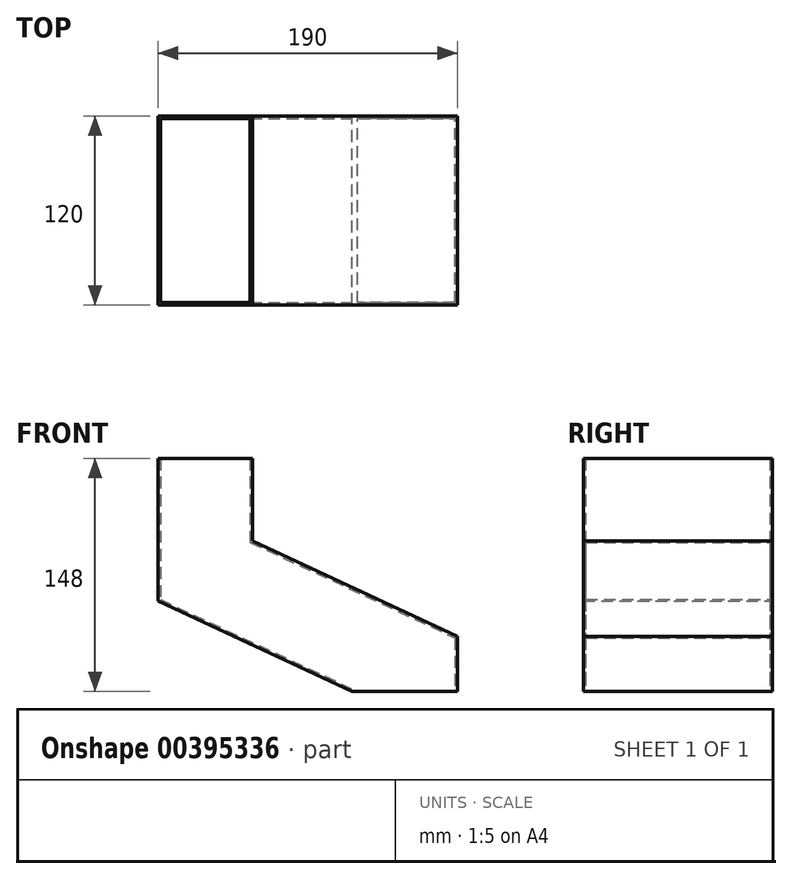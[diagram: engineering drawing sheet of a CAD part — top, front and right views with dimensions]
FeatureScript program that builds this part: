
annotation { "Feature Type Name" : "Feature", "Feature Type Description" : "" }
export const myFeature = defineFeature(function(context is Context, id is Id, definition is map)
    precondition{}
    {
        {
            var Q0;
            Q0=qCreatedBy(makeId("Front.planeOp"),FACE);
            var sketch = newSketch(context, id + "F0", { "sketchPlane" : qUnion([Q0])});
            skLineSegment(sketch, "E0.bottom", {"start": v(-176.51, 10) * mm, "end": v(-36.51, 10) * mm});
            skLineSegment(sketch, "E0.top", {"start": v(-176.51, 108) * mm, "end": v(-36.51, 108) * mm});
            skLineSegment(sketch, "E0.left", {"start": v(-176.51, 10) * mm, "end": v(-176.51, 108) * mm});
            skLineSegment(sketch, "E0.right", {"start": v(-36.51, 10) * mm, "end": v(-36.51, 108) * mm});
            skLineSegment(sketch, "E1.bottom", {"start": v(58.49, 42) * mm, "end": v(218.49, 42) * mm});
            skLineSegment(sketch, "E1.top", {"start": v(58.49, 108) * mm, "end": v(218.49, 108) * mm});
            skLineSegment(sketch, "E1.left", {"start": v(58.49, 42) * mm, "end": v(58.49, 108) * mm});
            skLineSegment(sketch, "E1.right", {"start": v(218.49, 42) * mm, "end": v(218.49, 108) * mm});
            skLineSegment(sketch, "E2.bottom", {"start": v(33.49, -40) * mm, "end": v(153.49, -40) * mm});
            skLineSegment(sketch, "E2.top", {"start": v(33.49, -10) * mm, "end": v(153.49, -10) * mm});
            skLineSegment(sketch, "E2.left", {"start": v(33.49, -40) * mm, "end": v(33.49, -10) * mm});
            skLineSegment(sketch, "E2.right", {"start": v(153.49, -40) * mm, "end": v(153.49, -10) * mm});
            skLineSegment(sketch, "E3", {"start": v(153.49, -40) * mm, "end": v(33.49, -40) * mm});
            skSolve(sketch);
        }
        {
            var Q0;
            Q0=qCreatedBy(makeId("Front.planeOp"),FACE);
            var sketch = newSketch(context, id + "F1", { "sketchPlane" : qUnion([Q0])});
            skPoint(sketch, "E4.0", {"position": v(-36.51, 108) * mm});
            skLineSegment(sketch, "E5", {"start": v(-36.51, 108) * mm, "end": v(23.49, 108) * mm});
            skLineSegment(sketch, "E6", {"start": v(153.49, -40) * mm, "end": v(86.57, -40) * mm});
            skLineSegment(sketch, "E7", {"start": v(23.49, 108) * mm, "end": v(23.49, 55.62) * mm});
            skLineSegment(sketch, "E8", {"start": v(153.49, -5) * mm, "end": v(153.49, -40) * mm});
            skLineSegment(sketch, "E9", {"start": v(23.49, 55.62) * mm, "end": v(153.49, -5) * mm});
            skLineSegment(sketch, "E10", {"start": v(-36.51, 108) * mm, "end": v(-36.51, 17.4) * mm});
            skLineSegment(sketch, "E11", {"start": v(-36.51, 17.4) * mm, "end": v(86.57, -40) * mm});
            skSolve(sketch);
        }
        {
            var Q0;
            Q0 = qSketchRegion(id + "F1", true);
            extrude(context, id + "F2", {"entities" : qUnion([Q0]), "depth" : 120 * mm});
        }
        {
            var Q0;
            Q0=makeQuery(id+"F2.opExtrude","SWEPT_FACE",FACE,{"disambiguationData":[OSD([sQuery(id+"F1.wireOp",EDGE,"E5")])]});
            var Q1;
            Q1=makeQuery(id+"F2.opExtrude","SWEPT_FACE",FACE,{"disambiguationData":[OSD([sQuery(id+"F1.wireOp",EDGE,"E6")])]});
            shell(context, id + "F3", {"entities" : qUnion([Q0, Q1]), "thickness" : 1.5 * mm});
        }
    });
